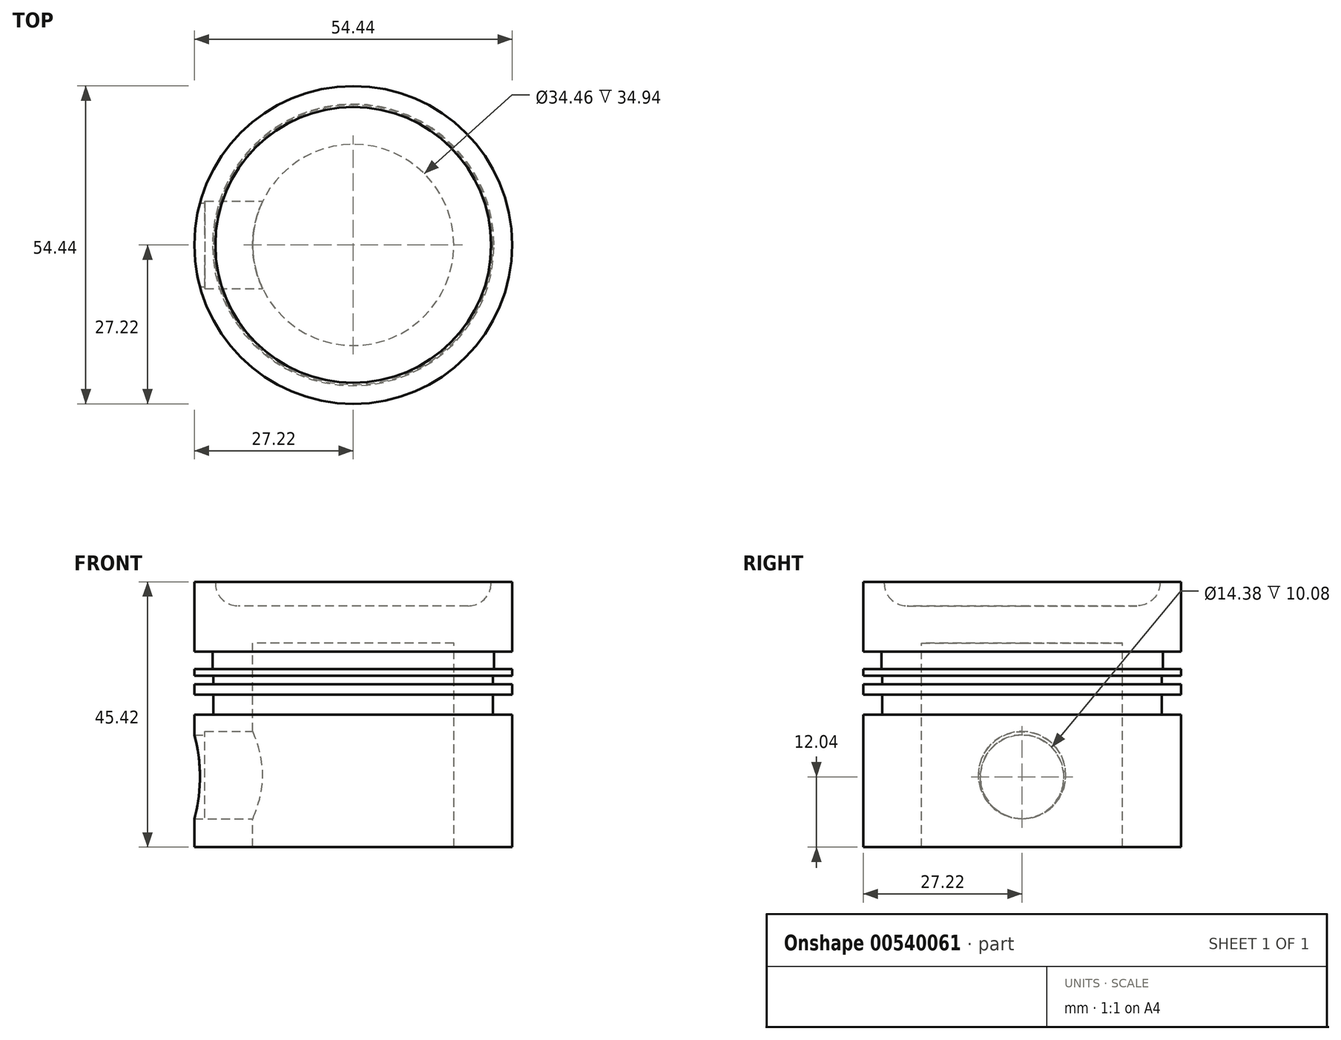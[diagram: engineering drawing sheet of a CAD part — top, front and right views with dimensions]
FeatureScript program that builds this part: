
annotation { "Feature Type Name" : "Feature", "Feature Type Description" : "" }
export const myFeature = defineFeature(function(context is Context, id is Id, definition is map)
    precondition{}
    {
        {
            var Q0;
            Q0=qCreatedBy(makeId("Front.planeOp"),FACE);
            var sketch = newSketch(context, id + "F0", { "sketchPlane" : qUnion([Q0])});
            skLineSegment(sketch, "E0.bottom", {"start": v(-17.23, 0) * mm, "end": v(-27.22, 0) * mm});
            skLineSegment(sketch, "E0.top", {"start": v(-23.61, 45.42) * mm, "end": v(-27.22, 45.42) * mm});
            skLineSegment(sketch, "E0.left", {"start": v(0, 34.94) * mm, "end": v(0, 41.33) * mm});
            skLineSegment(sketch, "E0.right", {"start": v(-27.22, 0) * mm, "end": v(-27.22, 22.7) * mm});
            skLineSegment(sketch, "E1", {"start": v(-19.68, 41.33) * mm, "end": v(0, 41.33) * mm});
            skArc(sketch, "E2", {"start": v(-23.61, 45.42) * mm, "mid": v(-22.52, 42.53) * mm, "end": v(-19.68, 41.33) * mm});
            skLineSegment(sketch, "E3", {"start": v(0, 34.94) * mm, "end": v(-17.23, 34.94) * mm});
            skLineSegment(sketch, "E4", {"start": v(-17.23, 34.94) * mm, "end": v(-17.23, 0) * mm});
            skLineSegment(sketch, "E5", {"start": v(0, 41.33) * mm, "end": v(0, 34.94) * mm});
            skLineSegment(sketch, "E6", {"start": v(-27.22, 33.47) * mm, "end": v(-24.1, 33.47) * mm});
            skLineSegment(sketch, "E7", {"start": v(-24.1, 33.47) * mm, "end": v(-24.1, 30.52) * mm});
            skLineSegment(sketch, "E8", {"start": v(-24.1, 30.52) * mm, "end": v(-27.22, 30.52) * mm});
            skLineSegment(sketch, "E9", {"start": v(-27.22, 30.52) * mm, "end": v(-27.22, 29.35) * mm});
            skLineSegment(sketch, "E10", {"start": v(-27.22, 26.1) * mm, "end": v(-23.94, 26.1) * mm});
            skLineSegment(sketch, "E11", {"start": v(-23.94, 26.1) * mm, "end": v(-23.94, 22.7) * mm});
            skPoint(sketch, "E11.endSnap0", {"position": v(-27.22, 22.7) * mm});
            skLineSegment(sketch, "E12", {"start": v(-23.94, 22.7) * mm, "end": v(-27.22, 22.7) * mm});
            skLineSegment(sketch, "E13", {"start": v(-27.22, 29.35) * mm, "end": v(-23.94, 29.35) * mm});
            skLineSegment(sketch, "E14", {"start": v(-23.94, 29.35) * mm, "end": v(-23.94, 27.88) * mm});
            skLineSegment(sketch, "E15", {"start": v(-23.94, 27.88) * mm, "end": v(-27.22, 27.88) * mm});
            skLineSegment(sketch, "E16.trimOffspring", {"start": v(-27.22, 33.47) * mm, "end": v(-27.22, 45.42) * mm});
            skLineSegment(sketch, "E17.trimOffspring", {"start": v(-27.22, 29.35) * mm, "end": v(-27.22, 30.52) * mm});
            skLineSegment(sketch, "E18.trimOffspring", {"start": v(-27.22, 27.88) * mm, "end": v(-27.22, 26.1) * mm});
            skLineSegment(sketch, "E19.trimOffspring", {"start": v(-27.22, 26.1) * mm, "end": v(-27.22, 27.88) * mm});
            skSolve(sketch);
        }
        {
            var Q0;
            Q0 = qSketchRegion(id + "F0", true);
            var Q1;
            Q1=sQuery(id+"F0.wireOp",EDGE,"E5");
            revolve(context, id + "F1", {"entities" : qUnion([Q0]), "axis" : qUnion([Q1]), "revolveType" : RevolveType.FULL});
        }
        {
            var Q0;
            Q0=qCreatedBy(makeId("Right.planeOp"),FACE);
            var sketch = newSketch(context, id + "F2", { "sketchPlane" : qUnion([Q0])});
            skCircle(sketch, "E20", {"center": v(0, 12.04) * mm, "radius": 7.19 * mm});
            skSolve(sketch);
        }
        {
            var Q0;
            Q0 = qSketchRegion(id + "F2", true);
            extrude(context, id + "F3", {"entities" : qUnion([Q0]), "operationType" : NewBodyOperationType.REMOVE, "oppositeDirection" : true, "depth" : 127 * mm, "offsetDistance" : 25.4 * mm});
        }
        {
            var Q0;
            Q0=qCreatedBy(makeId("Right.planeOp"),FACE);
            var sketch = newSketch(context, id + "F4", { "sketchPlane" : qUnion([Q0])});
            skCircle(sketch, "E21", {"center": v(0, 12.34) * mm, "radius": 7.48 * mm});
            skSolve(sketch);
        }
        {
            var Q0;
            Q0 = qSketchRegion(id + "F4", true);
            extrude(context, id + "F5", {"entities" : qUnion([Q0]), "operationType" : NewBodyOperationType.REMOVE, "oppositeDirection" : true, "depth" : 25.4 * mm, "offsetDistance" : 25.4 * mm});
        }
    });
